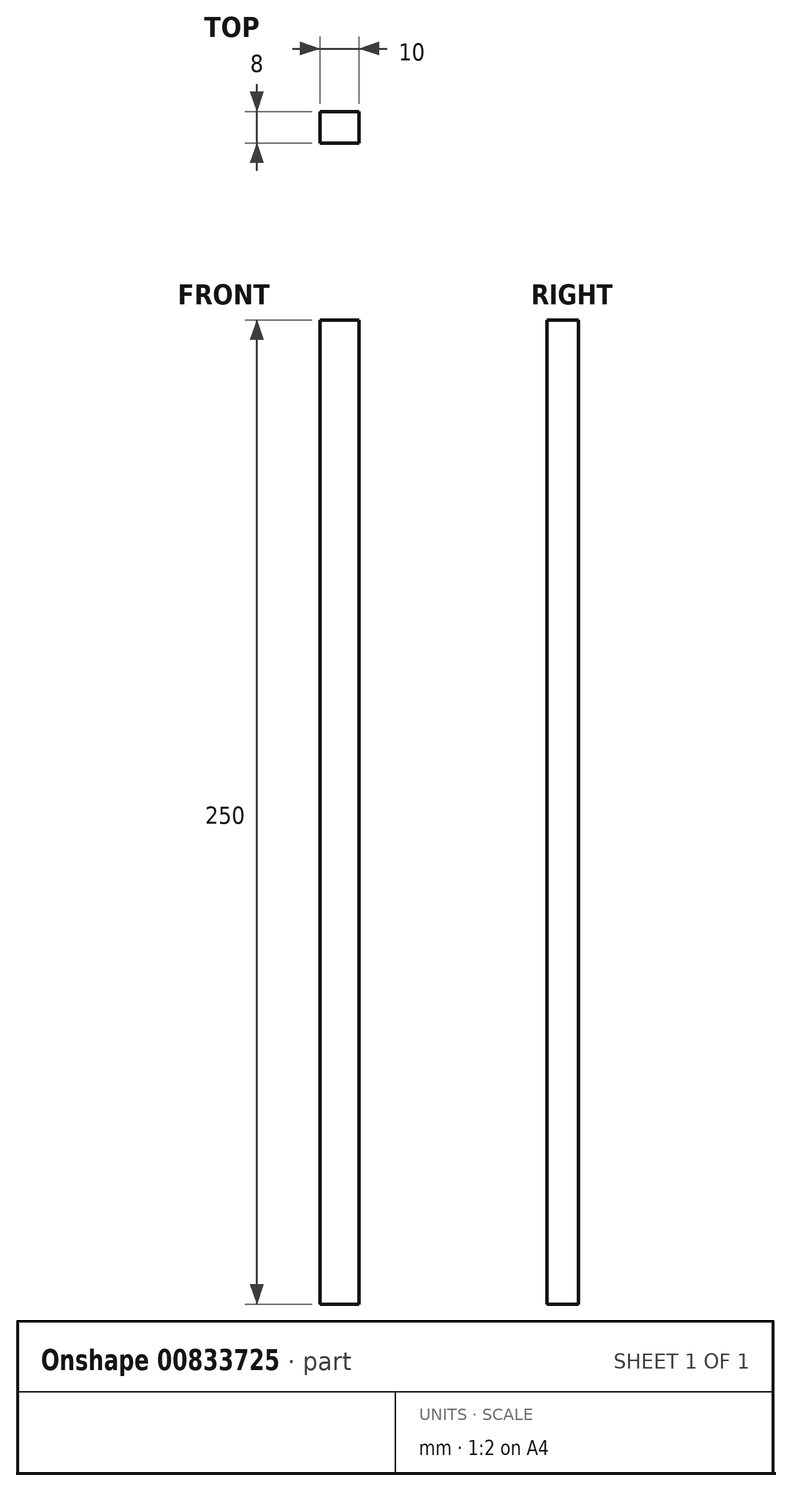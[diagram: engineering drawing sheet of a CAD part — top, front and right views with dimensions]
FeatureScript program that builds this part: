
annotation { "Feature Type Name" : "Feature", "Feature Type Description" : "" }
export const myFeature = defineFeature(function(context is Context, id is Id, definition is map)
    precondition{}
    {
        {
            var Q0;
            Q0=qCreatedBy(makeId("Top.planeOp"),FACE);
            var sketch = newSketch(context, id + "F0", { "sketchPlane" : qUnion([Q0])});
            skLineSegment(sketch, "E0", {"start": v(-66.36, 30.74) * mm, "end": v(-56.36, 30.74) * mm});
            skLineSegment(sketch, "E1", {"start": v(-66.36, 30.74) * mm, "end": v(-66.36, 22.74) * mm});
            skLineSegment(sketch, "E2", {"start": v(-56.36, 30.74) * mm, "end": v(-56.36, 22.74) * mm});
            skLineSegment(sketch, "E3", {"start": v(-66.36, 22.74) * mm, "end": v(-46.36, 22.74) * mm});
            skLineSegment(sketch, "E4", {"start": v(-56.36, 22.74) * mm, "end": v(-76.36, 22.74) * mm});
            skLineSegment(sketch, "E5", {"start": v(-46.36, 22.74) * mm, "end": v(-46.36, 2.74) * mm});
            skLineSegment(sketch, "E6", {"start": v(-76.36, 22.74) * mm, "end": v(-76.36, 2.74) * mm});
            skLineSegment(sketch, "E7", {"start": v(-46.36, 2.74) * mm, "end": v(-66.36, 2.74) * mm});
            skLineSegment(sketch, "E8", {"start": v(-76.36, 2.74) * mm, "end": v(-56.36, 2.74) * mm});
            skLineSegment(sketch, "E9", {"start": v(-66.36, 2.74) * mm, "end": v(-66.36, -5.26) * mm});
            skLineSegment(sketch, "E10", {"start": v(-56.36, 2.74) * mm, "end": v(-56.36, -5.26) * mm});
            skLineSegment(sketch, "E11", {"start": v(-66.36, -5.26) * mm, "end": v(-56.36, -5.26) * mm});
            skSolve(sketch);
        }
        {
            var Q0;
            Q0=makeQuery(id+"F0.imprint","IMPRINT",FACE,{"disambiguationData":[TD([[makeQuery(id+"F0.imprint","IMPRINT",EDGE,{"derivedFrom":sQuery(id+"F0.wireOp",EDGE,"E0")}),-1.0]])]});
            extrude(context, id + "F1", {"entities" : qUnion([Q0]), "depth" : 250 * mm, "offsetDistance" : 25 * mm});
        }
    });
